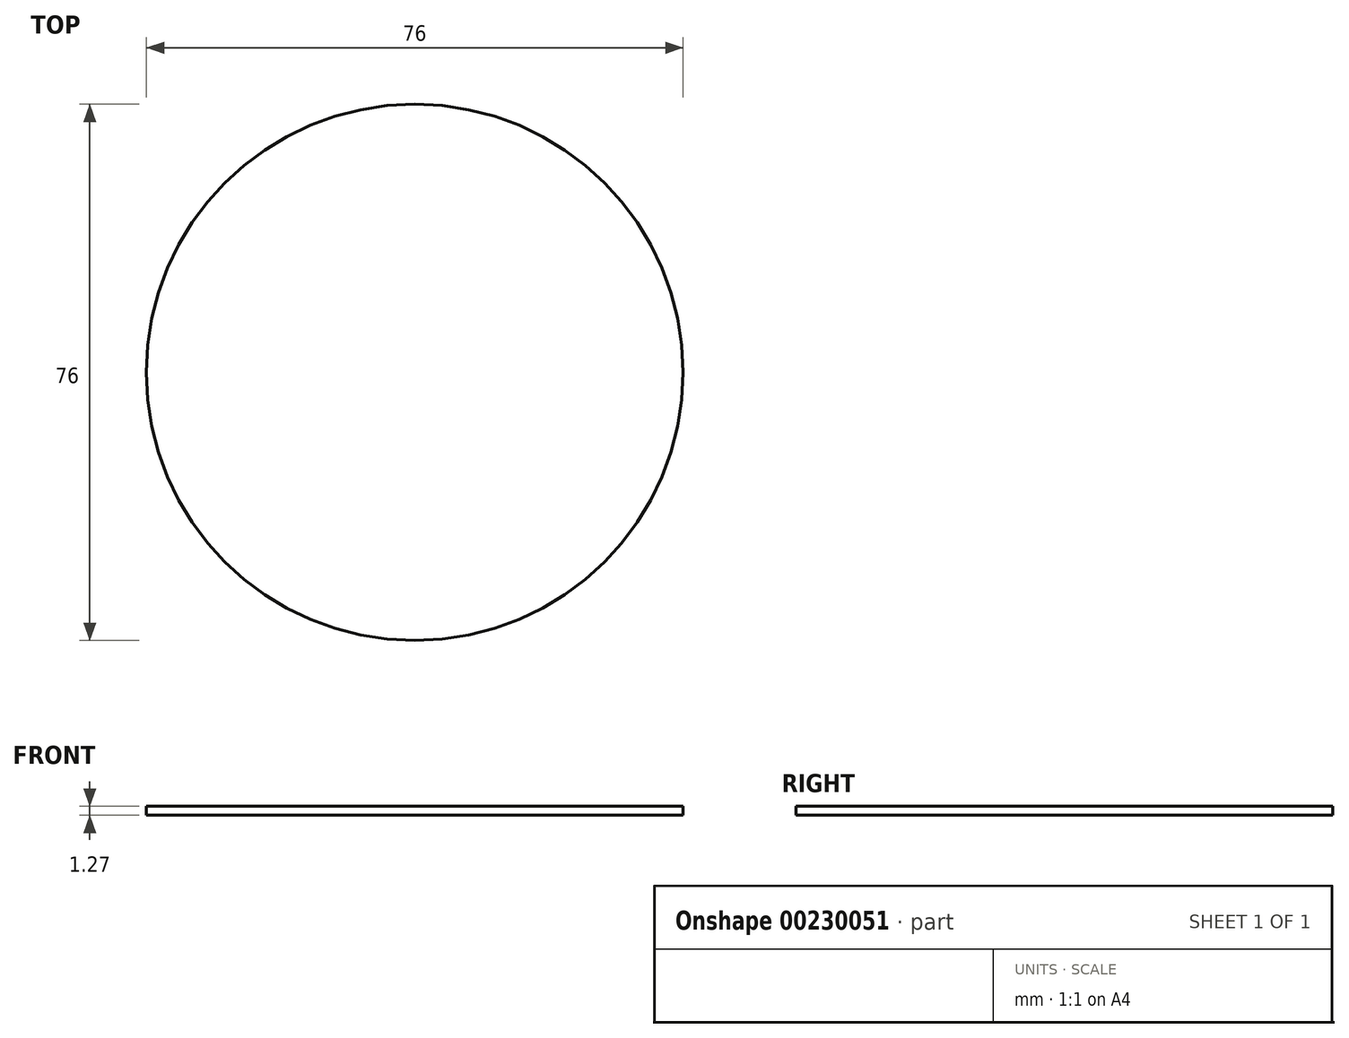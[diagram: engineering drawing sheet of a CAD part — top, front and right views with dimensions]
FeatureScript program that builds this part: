
annotation { "Feature Type Name" : "Feature", "Feature Type Description" : "" }
export const myFeature = defineFeature(function(context is Context, id is Id, definition is map)
    precondition{}
    {
        {
            var Q0;
            Q0=qCreatedBy(makeId("Top.planeOp"),FACE);
            var sketch = newSketch(context, id + "F0", { "sketchPlane" : qUnion([Q0])});
            skCircle(sketch, "E0", {"center": v(0, 0) * mm, "radius": 38 * mm});
            skSolve(sketch);
        }
        {
            var Q0;
            Q0=makeQuery(id+"F0.imprint","IMPRINT",FACE,{"disambiguationData":[TD([[makeQuery(id+"F0.imprint","IMPRINT",EDGE,{"derivedFrom":sQuery(id+"F0.wireOp",EDGE,"E0")}),1.0]])]});
            extrude(context, id + "F1", {"entities" : qUnion([Q0]), "depth" : 1.27 * mm});
        }
    });
